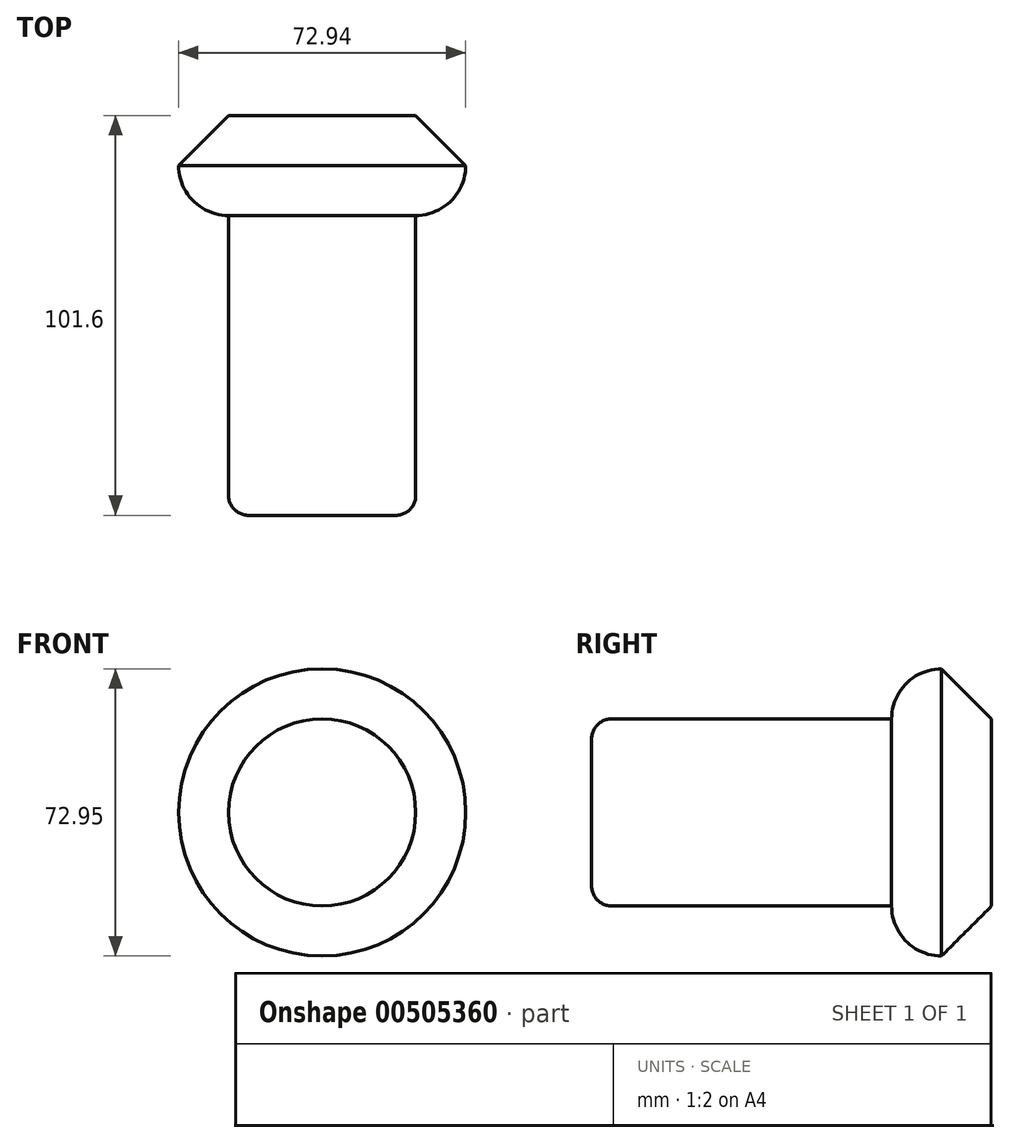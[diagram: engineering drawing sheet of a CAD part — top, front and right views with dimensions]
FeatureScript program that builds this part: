
annotation { "Feature Type Name" : "Feature", "Feature Type Description" : "" }
export const myFeature = defineFeature(function(context is Context, id is Id, definition is map)
    precondition{}
    {
        {
            var Q0;
            Q0=qCreatedBy(makeId("Front.planeOp"),FACE);
            var sketch = newSketch(context, id + "F0", { "sketchPlane" : qUnion([Q0])});
            skCircle(sketch, "E0", {"center": v(27.8, -14.2) * mm, "radius": 36.47 * mm});
            skSolve(sketch);
        }
        {
            var Q0;
            Q0=makeQuery(id+"F0.imprint","IMPRINT",FACE,{"disambiguationData":[TD([[makeQuery(id+"F0.imprint","IMPRINT",EDGE,{"derivedFrom":sQuery(id+"F0.wireOp",EDGE,"E0")}),1.0]])]});
            var sketch = newSketch(context, id + "F1", { "sketchPlane" : qUnion([Q0])});
            skSolve(sketch);
        }
        {
            var Q0;
            Q0=makeQuery(id+"F1.imprint","IMPRINT",FACE,{"disambiguationData":[TD([[makeQuery(id+"F1.imprint","IMPRINT",EDGE,{"derivedFrom":makeQuery(id+"F0.imprint","IMPRINT",EDGE,{"derivedFrom":sQuery(id+"F0.wireOp",EDGE,"E0")})}),1.0]])]});
            extrude(context, id + "F2", {"entities" : qUnion([Q0]), "oppositeDirection" : true, "depth" : 25.4 * mm, "offsetDistance" : 25.4 * mm});
        }
        {
            var Q0;
            Q0=makeQuery(id+"F2.opExtrude","CAP_EDGE",EDGE,{"disambiguationData":[OSD([sQuery(id+"F0.wireOp",EDGE,"E0")])],"isStart":false});
            chamfer(context, id + "F3", {"entities" : qUnion([Q0]), "width" : 12.7 * mm, "tangentPropagation" : true});
        }
        {
            var Q0;
            Q0=makeQuery(id+"F2.opExtrude","CAP_FACE",FACE,{"disambiguationData":[OSD([sQuery(id+"F0.wireOp",EDGE,"E0")])],"isStart":true});
            fillet(context, id + "F4", {"entities" : qUnion([Q0]), "radius" : 12.7 * mm, "tangentPropagation" : true, "allowEdgeOverflow" : false});
        }
        {
            var Q0;
            Q0=makeQuery(id+"F2.opExtrude","CAP_FACE",FACE,{"disambiguationData":[OSD([sQuery(id+"F0.wireOp",EDGE,"E0")])],"isStart":false});
            var sketch = newSketch(context, id + "F5", { "sketchPlane" : qUnion([Q0])});
            skSolve(sketch);
        }
        {
            var Q0;
            {var subQ0=sQuery(id+"F0.wireOp",EDGE,"E0");Q0=makeQuery(id+"F5.imprint","IMPRINT",FACE,{"disambiguationData":[TD([[makeQuery(id+"F5.imprint","IMPRINT",EDGE,{"derivedFrom":makeQuery(id+"F3.opChamfer","BLEND_EDGE",EDGE,{"blendedFrom":[makeQuery(id+"F2.opExtrude","CAP_EDGE",EDGE,{"disambiguationData":[OSD([subQ0])],"isStart":false}),makeQuery(id+"F2.opExtrude","CAP_FACE",FACE,{"disambiguationData":[OSD([subQ0])],"isStart":false})],"blendedInto":[makeQuery(id+"F2.opExtrude","CAP_FACE",FACE,{"disambiguationData":[OSD([subQ0])],"isStart":false})]})}),1.0]])]});}
            extrude(context, id + "F6", {"entities" : qUnion([Q0]), "operationType" : NewBodyOperationType.ADD, "oppositeDirection" : true, "depth" : 101.6 * mm, "offsetDistance" : 25.4 * mm});
        }
        {
            var Q0;
            Q0=makeQuery(id+"F6.opExtrude","CAP_FACE",FACE,{"disambiguationData":[OSD([sQuery(id+"F0.wireOp",EDGE,"E0")])],"isStart":false});
            fillet(context, id + "F7", {"entities" : qUnion([Q0]), "radius" : 5.08 * mm, "tangentPropagation" : true, "allowEdgeOverflow" : false});
        }
    });
